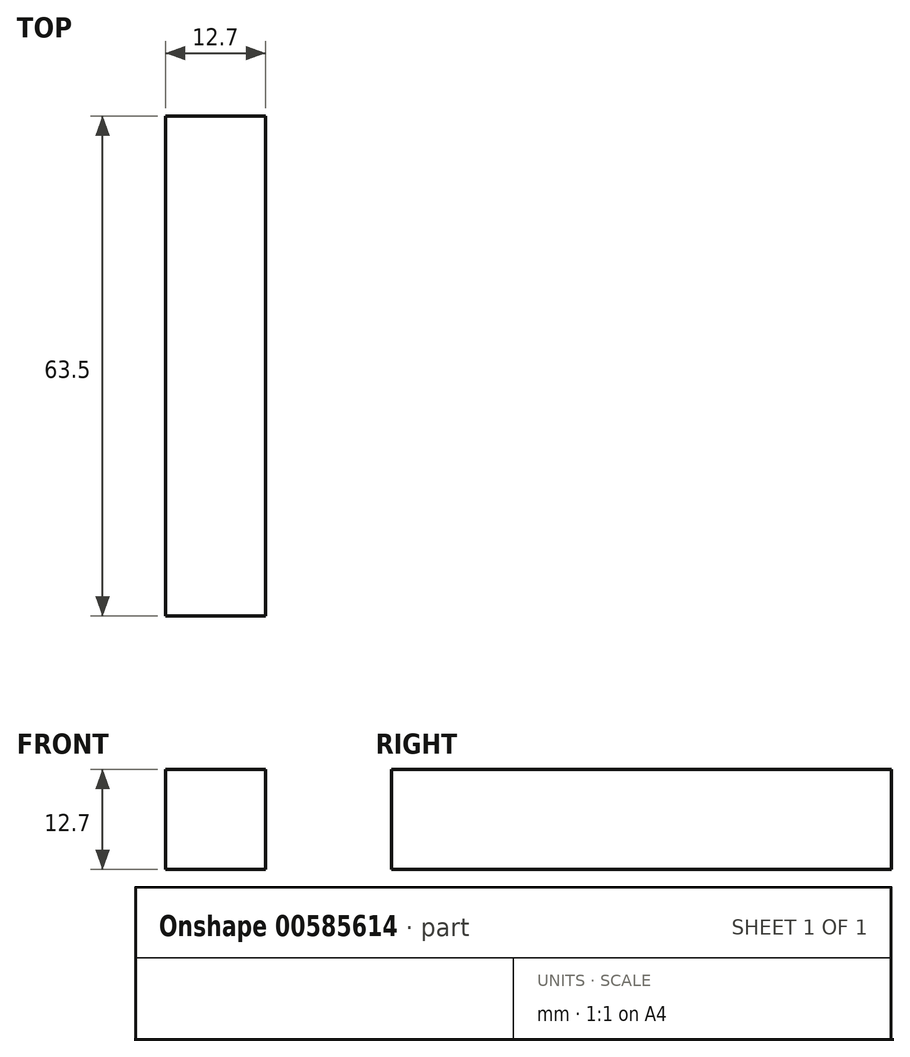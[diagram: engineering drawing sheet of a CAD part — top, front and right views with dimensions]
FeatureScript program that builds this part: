
annotation { "Feature Type Name" : "Feature", "Feature Type Description" : "" }
export const myFeature = defineFeature(function(context is Context, id is Id, definition is map)
    precondition{}
    {
        {
            var Q0;
            Q0=qCreatedBy(makeId("Top.planeOp"),FACE);
            var sketch = newSketch(context, id + "F0", { "sketchPlane" : qUnion([Q0])});
            skLineSegment(sketch, "E0.bottom", {"start": v(-6.35, 31.75) * mm, "end": v(6.35, 31.75) * mm});
            skLineSegment(sketch, "E0.top", {"start": v(-6.35, -31.75) * mm, "end": v(6.35, -31.75) * mm});
            skLineSegment(sketch, "E0.left", {"start": v(-6.35, 31.75) * mm, "end": v(-6.35, -31.75) * mm});
            skLineSegment(sketch, "E0.right", {"start": v(6.35, 31.75) * mm, "end": v(6.35, -31.75) * mm});
            skPoint(sketch, "E0.middle", {"position": v(0, 0) * mm});
            skSolve(sketch);
        }
        {
            var Q0;
            Q0=makeQuery(id+"F0.imprint","IMPRINT",FACE,{"disambiguationData":[TD([[makeQuery(id+"F0.imprint","IMPRINT",EDGE,{"derivedFrom":sQuery(id+"F0.wireOp",EDGE,"E0.bottom")}),-1.0]])]});
            extrude(context, id + "F1", {"entities" : qUnion([Q0]), "depth" : 12.7 * mm, "offsetDistance" : 25.4 * mm});
        }
    });
